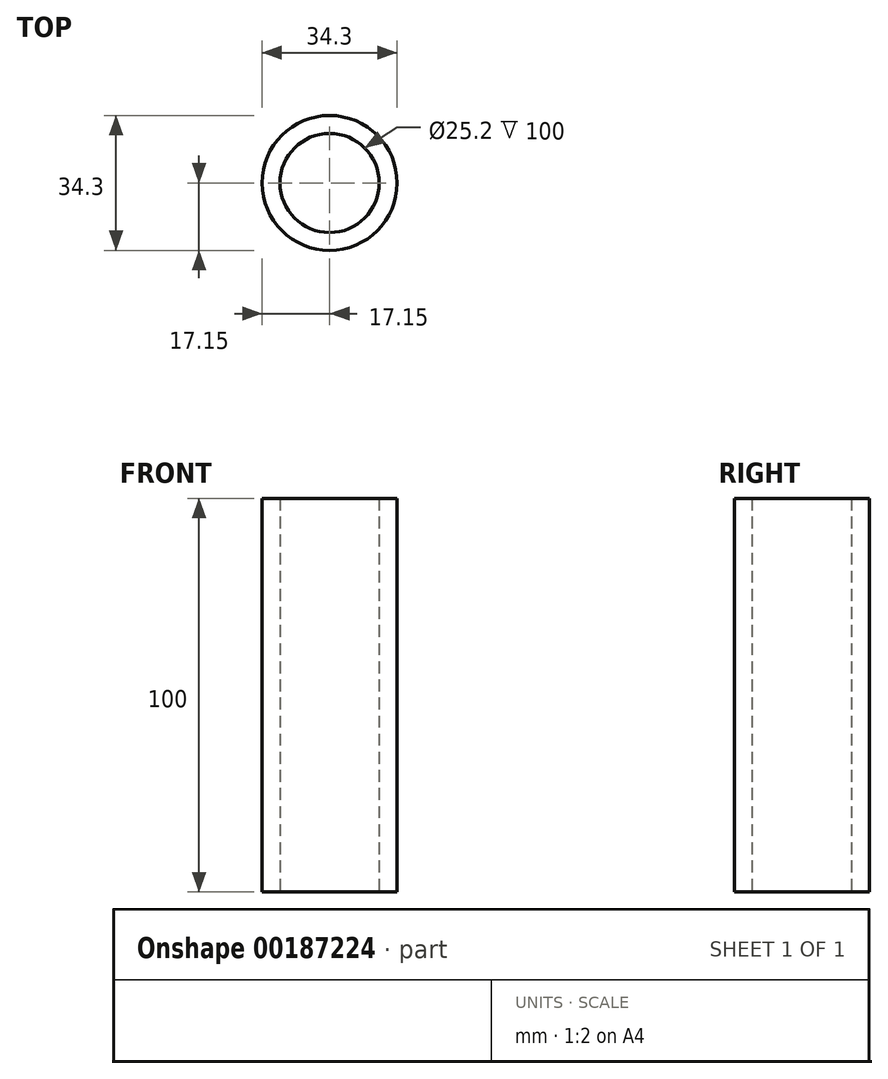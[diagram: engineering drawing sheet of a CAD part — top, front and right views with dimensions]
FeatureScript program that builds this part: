
annotation { "Feature Type Name" : "Feature", "Feature Type Description" : "" }
export const myFeature = defineFeature(function(context is Context, id is Id, definition is map)
    precondition{}
    {
        {
            var Q0;
            Q0=qCreatedBy(makeId("Top.planeOp"),FACE);
            var sketch = newSketch(context, id + "F0", { "sketchPlane" : qUnion([Q0])});
            skCircle(sketch, "E0", {"center": v(0, 0) * mm, "radius": 17.14 * mm});
            skCircle(sketch, "E1", {"center": v(0, 0) * mm, "radius": 12.6 * mm});
            skSolve(sketch);
        }
        {
            var Q0;
            Q0 = qSketchRegion(id + "F0", true);
            extrude(context, id + "F1", {"entities" : qUnion([Q0]), "depth" : 100 * mm});
        }
    });
